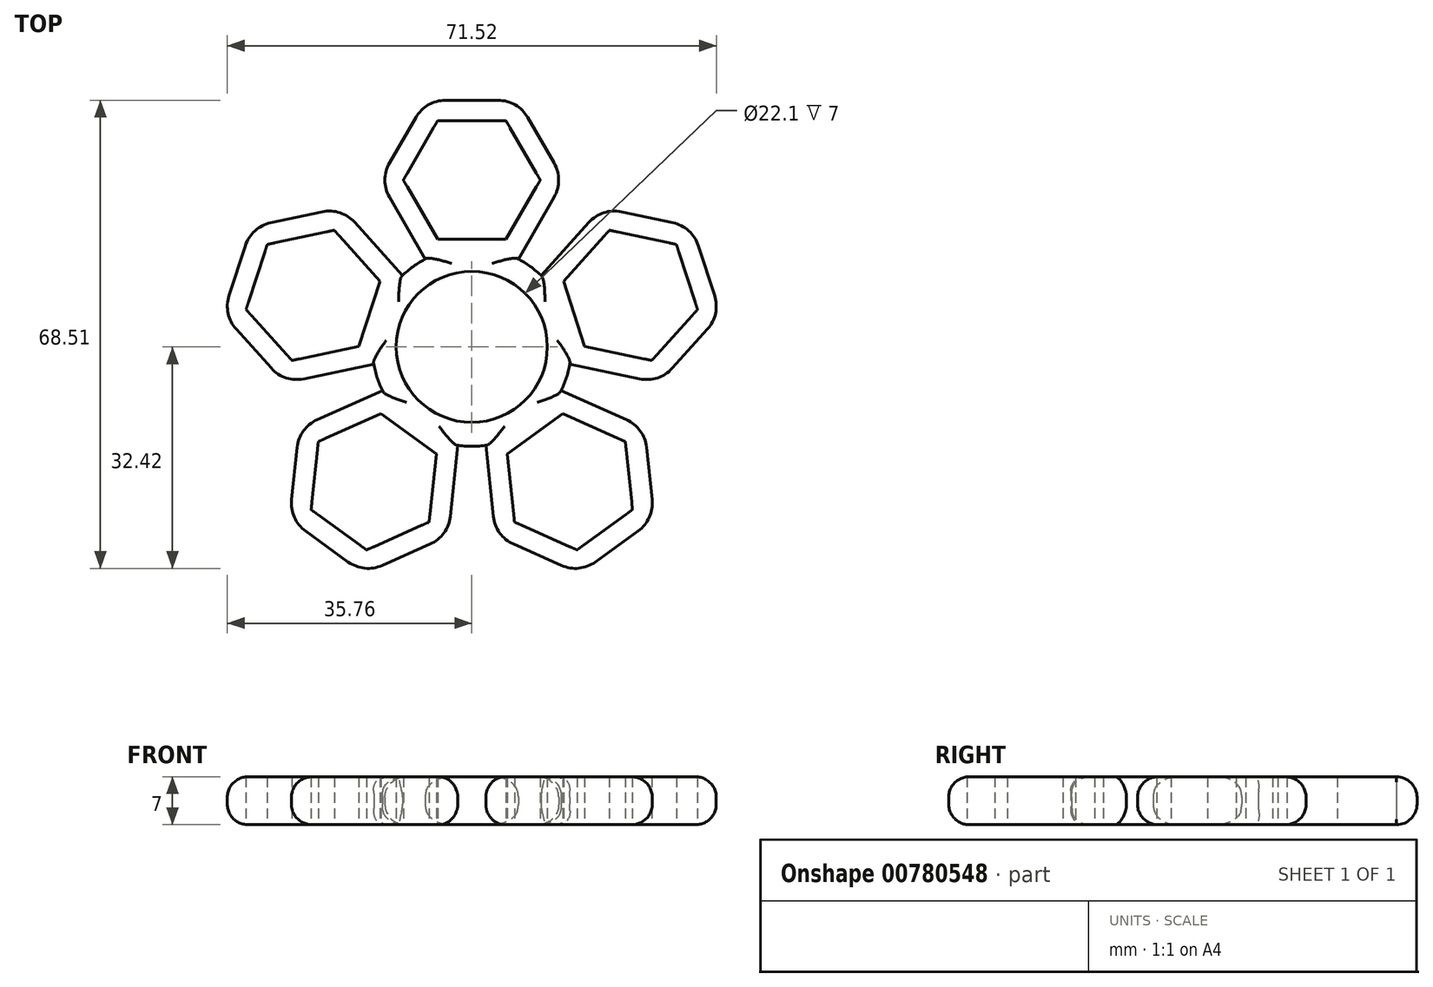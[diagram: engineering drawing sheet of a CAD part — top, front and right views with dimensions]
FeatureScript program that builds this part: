
annotation { "Feature Type Name" : "Feature", "Feature Type Description" : "" }
export const myFeature = defineFeature(function(context is Context, id is Id, definition is map)
    precondition{}
    {
        {
            var Q0;
            Q0=qCreatedBy(makeId("Top.planeOp"),FACE);
            var sketch = newSketch(context, id + "F0", { "sketchPlane" : qUnion([Q0])});
            skCircle(sketch, "E0", {"center": v(0, 0) * mm, "radius": 11.05 * mm});
            skCircle(sketch, "E1.0", {"center": v(0, 0) * mm, "radius": 14.55 * mm});
            skCircle(sketch, "E2.cCircle", {"center": v(0, 0) * mm, "radius": 19.75 * mm, "construction": true});
            skLineSegment(sketch, "E2.0", {"start": v(-23.22, 7.54) * mm, "end": v(0, 24.41) * mm, "construction": true});
            skLineSegment(sketch, "E2.1", {"start": v(0, 24.41) * mm, "end": v(23.22, 7.54) * mm, "construction": true});
            skLineSegment(sketch, "E2.2", {"start": v(23.22, 7.54) * mm, "end": v(14.35, -19.75) * mm, "construction": true});
            skLineSegment(sketch, "E2.3", {"start": v(14.35, -19.75) * mm, "end": v(-14.35, -19.75) * mm, "construction": true});
            skLineSegment(sketch, "E2.4", {"start": v(-14.35, -19.75) * mm, "end": v(-23.22, 7.54) * mm, "construction": true});
            skPoint(sketch, "E2.0.midPoint", {"position": v(-11.6, 15.98) * mm});
            skCircle(sketch, "E3.cCircle", {"center": v(0, 24.41) * mm, "radius": 8.68 * mm, "construction": true});
            skLineSegment(sketch, "E3.0", {"start": v(-5, 33.09) * mm, "end": v(5, 33.09) * mm});
            skLineSegment(sketch, "E3.1", {"start": v(5, 33.09) * mm, "end": v(10.02, 24.41) * mm});
            skLineSegment(sketch, "E3.2", {"start": v(10.02, 24.41) * mm, "end": v(5, 15.74) * mm});
            skLineSegment(sketch, "E3.3", {"start": v(5, 15.74) * mm, "end": v(-5, 15.74) * mm});
            skLineSegment(sketch, "E3.4", {"start": v(-5, 15.74) * mm, "end": v(-10.02, 24.41) * mm});
            skLineSegment(sketch, "E3.5", {"start": v(-10.02, 24.41) * mm, "end": v(-5, 33.09) * mm});
            skPoint(sketch, "E3.0.midPoint", {"position": v(0, 33.09) * mm});
            skCircle(sketch, "E4.cCircle", {"center": v(-23.22, 7.54) * mm, "radius": 8.68 * mm, "construction": true});
            skLineSegment(sketch, "E4.0", {"start": v(-33.02, 5.46) * mm, "end": v(-29.92, 14.99) * mm});
            skLineSegment(sketch, "E4.1", {"start": v(-29.92, 14.99) * mm, "end": v(-20.12, 17.07) * mm});
            skLineSegment(sketch, "E4.2", {"start": v(-20.12, 17.07) * mm, "end": v(-13.42, 9.63) * mm});
            skLineSegment(sketch, "E4.3", {"start": v(-13.42, 9.63) * mm, "end": v(-16.51, 0.1) * mm});
            skLineSegment(sketch, "E4.4", {"start": v(-16.51, 0.1) * mm, "end": v(-26.31, -1.98) * mm});
            skLineSegment(sketch, "E4.5", {"start": v(-26.31, -1.98) * mm, "end": v(-33.02, 5.46) * mm});
            skPoint(sketch, "E4.0.midPoint", {"position": v(-31.47, 10.22) * mm});
            skCircle(sketch, "E5.cCircle", {"center": v(-14.35, -19.75) * mm, "radius": 8.68 * mm, "construction": true});
            skLineSegment(sketch, "E5.0", {"start": v(-15.4, -29.71) * mm, "end": v(-23.5, -23.82) * mm});
            skLineSegment(sketch, "E5.1", {"start": v(-23.5, -23.82) * mm, "end": v(-22.45, -13.86) * mm});
            skLineSegment(sketch, "E5.2", {"start": v(-22.45, -13.86) * mm, "end": v(-13.3, -9.79) * mm});
            skLineSegment(sketch, "E5.3", {"start": v(-13.3, -9.79) * mm, "end": v(-5.2, -15.68) * mm});
            skLineSegment(sketch, "E5.4", {"start": v(-5.2, -15.68) * mm, "end": v(-6.25, -25.64) * mm});
            skLineSegment(sketch, "E5.5", {"start": v(-6.25, -25.64) * mm, "end": v(-15.4, -29.71) * mm});
            skPoint(sketch, "E5.0.midPoint", {"position": v(-19.45, -26.77) * mm});
            skCircle(sketch, "E6.cCircle", {"center": v(14.35, -19.75) * mm, "radius": 8.68 * mm, "construction": true});
            skLineSegment(sketch, "E6.0", {"start": v(23.5, -23.82) * mm, "end": v(15.4, -29.71) * mm});
            skLineSegment(sketch, "E6.1", {"start": v(15.4, -29.71) * mm, "end": v(6.25, -25.64) * mm});
            skLineSegment(sketch, "E6.2", {"start": v(6.25, -25.64) * mm, "end": v(5.2, -15.68) * mm});
            skLineSegment(sketch, "E6.3", {"start": v(5.2, -15.68) * mm, "end": v(13.3, -9.79) * mm});
            skLineSegment(sketch, "E6.4", {"start": v(13.3, -9.79) * mm, "end": v(22.45, -13.86) * mm});
            skLineSegment(sketch, "E6.5", {"start": v(22.45, -13.86) * mm, "end": v(23.5, -23.82) * mm});
            skPoint(sketch, "E6.0.midPoint", {"position": v(19.45, -26.77) * mm});
            skCircle(sketch, "E7.cCircle", {"center": v(23.22, 7.54) * mm, "radius": 8.68 * mm, "construction": true});
            skLineSegment(sketch, "E7.0", {"start": v(29.92, 14.99) * mm, "end": v(33.02, 5.46) * mm});
            skLineSegment(sketch, "E7.1", {"start": v(33.02, 5.46) * mm, "end": v(26.31, -1.98) * mm});
            skLineSegment(sketch, "E7.2", {"start": v(26.31, -1.98) * mm, "end": v(16.51, 0.1) * mm});
            skLineSegment(sketch, "E7.3", {"start": v(16.51, 0.1) * mm, "end": v(13.42, 9.63) * mm});
            skLineSegment(sketch, "E7.4", {"start": v(13.42, 9.63) * mm, "end": v(20.12, 17.07) * mm});
            skLineSegment(sketch, "E7.5", {"start": v(20.12, 17.07) * mm, "end": v(29.92, 14.99) * mm});
            skPoint(sketch, "E7.0.midPoint", {"position": v(31.47, 10.22) * mm});
            skLineSegment(sketch, "E8.0", {"start": v(10.03, 10.35) * mm, "end": v(19.05, 20.37) * mm});
            skLineSegment(sketch, "E8.1", {"start": v(32.24, 17.56) * mm, "end": v(36.4, 4.74) * mm});
            skLineSegment(sketch, "E8.2", {"start": v(36.4, 4.74) * mm, "end": v(27.38, -5.28) * mm});
            skLineSegment(sketch, "E8.3", {"start": v(19.05, 20.37) * mm, "end": v(32.24, 17.56) * mm});
            skLineSegment(sketch, "E8.4", {"start": v(27.38, -5.28) * mm, "end": v(14.2, -2.47) * mm});
            skLineSegment(sketch, "E8.5", {"start": v(14.2, -2.47) * mm, "end": v(10.03, 10.35) * mm});
            skLineSegment(sketch, "E9.0", {"start": v(-13.48, 24.41) * mm, "end": v(-6.74, 36.09) * mm});
            skLineSegment(sketch, "E9.1", {"start": v(6.74, 36.09) * mm, "end": v(13.48, 24.41) * mm});
            skLineSegment(sketch, "E9.2", {"start": v(13.48, 24.41) * mm, "end": v(6.74, 12.74) * mm});
            skLineSegment(sketch, "E9.3", {"start": v(-6.74, 36.09) * mm, "end": v(6.74, 36.09) * mm});
            skLineSegment(sketch, "E9.4", {"start": v(6.74, 12.74) * mm, "end": v(-6.74, 12.74) * mm});
            skLineSegment(sketch, "E9.5", {"start": v(-6.74, 12.74) * mm, "end": v(-13.48, 24.41) * mm});
            skLineSegment(sketch, "E10.0", {"start": v(-36.4, 4.74) * mm, "end": v(-32.24, 17.56) * mm});
            skLineSegment(sketch, "E10.1", {"start": v(-19.05, 20.37) * mm, "end": v(-10.03, 10.35) * mm});
            skLineSegment(sketch, "E10.2", {"start": v(-10.03, 10.35) * mm, "end": v(-14.2, -2.47) * mm});
            skLineSegment(sketch, "E10.3", {"start": v(-32.24, 17.56) * mm, "end": v(-19.05, 20.37) * mm});
            skLineSegment(sketch, "E10.4", {"start": v(-14.2, -2.47) * mm, "end": v(-27.38, -5.28) * mm});
            skLineSegment(sketch, "E10.5", {"start": v(-27.38, -5.28) * mm, "end": v(-36.4, 4.74) * mm});
            skLineSegment(sketch, "E11.0", {"start": v(-26.66, -25.23) * mm, "end": v(-25.26, -11.83) * mm});
            skLineSegment(sketch, "E11.1", {"start": v(-12.94, -6.34) * mm, "end": v(-2.03, -14.27) * mm});
            skLineSegment(sketch, "E11.2", {"start": v(-2.03, -14.27) * mm, "end": v(-3.44, -27.67) * mm});
            skLineSegment(sketch, "E11.3", {"start": v(-25.26, -11.83) * mm, "end": v(-12.94, -6.34) * mm});
            skLineSegment(sketch, "E11.4", {"start": v(-3.44, -27.67) * mm, "end": v(-15.76, -33.16) * mm});
            skLineSegment(sketch, "E11.5", {"start": v(-15.76, -33.16) * mm, "end": v(-26.66, -25.23) * mm});
            skLineSegment(sketch, "E12.0", {"start": v(3.44, -27.67) * mm, "end": v(2.03, -14.27) * mm});
            skLineSegment(sketch, "E12.1", {"start": v(12.94, -6.34) * mm, "end": v(25.26, -11.83) * mm});
            skLineSegment(sketch, "E12.2", {"start": v(25.26, -11.83) * mm, "end": v(26.66, -25.23) * mm});
            skLineSegment(sketch, "E12.3", {"start": v(2.03, -14.27) * mm, "end": v(12.94, -6.34) * mm});
            skLineSegment(sketch, "E12.4", {"start": v(26.66, -25.23) * mm, "end": v(15.76, -33.16) * mm});
            skLineSegment(sketch, "E12.5", {"start": v(15.76, -33.16) * mm, "end": v(3.44, -27.67) * mm});
            skSolve(sketch);
        }
        {
            var Q0;
            Q0=qSketchRegion(id+"F0",true);
            extrude(context, id + "F1", {"entities" : qUnion([Q0]), "depth" : 7 * mm, "offsetDistance" : 25 * mm});
        }
        {
            var Q0;
            Q0=makeQuery(id+"F1.opExtrude","SWEPT_EDGE",EDGE,{"disambiguationData":[OSD([sQuery(id+"F0.wireOp",EDGE,"E12.0"),sQuery(id+"F0.wireOp",EDGE,"E12.5")])]});
            var Q1;
            Q1=makeQuery(id+"F1.opExtrude","SWEPT_EDGE",EDGE,{"disambiguationData":[OSD([sQuery(id+"F0.wireOp",EDGE,"E12.2"),sQuery(id+"F0.wireOp",EDGE,"E12.4")])]});
            var Q2;
            Q2=makeQuery(id+"F1.opExtrude","SWEPT_EDGE",EDGE,{"disambiguationData":[OSD([sQuery(id+"F0.wireOp",EDGE,"E12.1"),sQuery(id+"F0.wireOp",EDGE,"E12.2")])]});
            var Q3;
            Q3=makeQuery(id+"F1.opExtrude","SWEPT_EDGE",EDGE,{"disambiguationData":[OSD([sQuery(id+"F0.wireOp",EDGE,"E8.2"),sQuery(id+"F0.wireOp",EDGE,"E8.4")])]});
            var Q4;
            Q4=makeQuery(id+"F1.opExtrude","SWEPT_EDGE",EDGE,{"disambiguationData":[OSD([sQuery(id+"F0.wireOp",EDGE,"E8.1"),sQuery(id+"F0.wireOp",EDGE,"E8.2")])]});
            var Q5;
            Q5=makeQuery(id+"F1.opExtrude","SWEPT_EDGE",EDGE,{"disambiguationData":[OSD([sQuery(id+"F0.wireOp",EDGE,"E8.1"),sQuery(id+"F0.wireOp",EDGE,"E8.3")])]});
            var Q6;
            Q6=makeQuery(id+"F1.opExtrude","SWEPT_EDGE",EDGE,{"disambiguationData":[OSD([sQuery(id+"F0.wireOp",EDGE,"E8.0"),sQuery(id+"F0.wireOp",EDGE,"E8.3")])]});
            var Q7;
            Q7=makeQuery(id+"F1.opExtrude","SWEPT_EDGE",EDGE,{"disambiguationData":[OSD([sQuery(id+"F0.wireOp",EDGE,"E9.1"),sQuery(id+"F0.wireOp",EDGE,"E9.2")])]});
            var Q8;
            Q8=makeQuery(id+"F1.opExtrude","SWEPT_EDGE",EDGE,{"disambiguationData":[OSD([sQuery(id+"F0.wireOp",EDGE,"E9.1"),sQuery(id+"F0.wireOp",EDGE,"E9.3")])]});
            var Q9;
            Q9=makeQuery(id+"F1.opExtrude","SWEPT_EDGE",EDGE,{"disambiguationData":[OSD([sQuery(id+"F0.wireOp",EDGE,"E9.0"),sQuery(id+"F0.wireOp",EDGE,"E9.3")])]});
            var Q10;
            Q10=makeQuery(id+"F1.opExtrude","SWEPT_EDGE",EDGE,{"disambiguationData":[OSD([sQuery(id+"F0.wireOp",EDGE,"E9.0"),sQuery(id+"F0.wireOp",EDGE,"E9.5")])]});
            var Q11;
            Q11=makeQuery(id+"F1.opExtrude","SWEPT_EDGE",EDGE,{"disambiguationData":[OSD([sQuery(id+"F0.wireOp",EDGE,"E10.1"),sQuery(id+"F0.wireOp",EDGE,"E10.3")])]});
            var Q12;
            Q12=makeQuery(id+"F1.opExtrude","SWEPT_EDGE",EDGE,{"disambiguationData":[OSD([sQuery(id+"F0.wireOp",EDGE,"E10.0"),sQuery(id+"F0.wireOp",EDGE,"E10.3")])]});
            var Q13;
            Q13=makeQuery(id+"F1.opExtrude","SWEPT_EDGE",EDGE,{"disambiguationData":[OSD([sQuery(id+"F0.wireOp",EDGE,"E10.0"),sQuery(id+"F0.wireOp",EDGE,"E10.5")])]});
            var Q14;
            Q14=makeQuery(id+"F1.opExtrude","SWEPT_EDGE",EDGE,{"disambiguationData":[OSD([sQuery(id+"F0.wireOp",EDGE,"E10.4"),sQuery(id+"F0.wireOp",EDGE,"E10.5")])]});
            var Q15;
            Q15=makeQuery(id+"F1.opExtrude","SWEPT_EDGE",EDGE,{"disambiguationData":[OSD([sQuery(id+"F0.wireOp",EDGE,"E11.0"),sQuery(id+"F0.wireOp",EDGE,"E11.3")])]});
            var Q16;
            Q16=makeQuery(id+"F1.opExtrude","SWEPT_EDGE",EDGE,{"disambiguationData":[OSD([sQuery(id+"F0.wireOp",EDGE,"E11.0"),sQuery(id+"F0.wireOp",EDGE,"E11.5")])]});
            var Q17;
            Q17=makeQuery(id+"F1.opExtrude","SWEPT_EDGE",EDGE,{"disambiguationData":[OSD([sQuery(id+"F0.wireOp",EDGE,"E11.4"),sQuery(id+"F0.wireOp",EDGE,"E11.5")])]});
            var Q18;
            Q18=makeQuery(id+"F1.opExtrude","SWEPT_EDGE",EDGE,{"disambiguationData":[OSD([sQuery(id+"F0.wireOp",EDGE,"E11.2"),sQuery(id+"F0.wireOp",EDGE,"E11.4")])]});
            var Q19;
            Q19=makeQuery(id+"F1.opExtrude","SWEPT_EDGE",EDGE,{"disambiguationData":[OSD([sQuery(id+"F0.wireOp",EDGE,"E12.4"),sQuery(id+"F0.wireOp",EDGE,"E12.5")])]});
            fillet(context, id + "F2", {"entities" : qUnion([Q0, Q1, Q2, Q3, Q4, Q5, Q6, Q7, Q8, Q9, Q10, Q11, Q12, Q13, Q14, Q15, Q16, Q17, Q18, Q19]), "radius" : 5 * mm, "tangentPropagation" : true, "allowEdgeOverflow" : false});
        }
        {
            var Q0;
            Q0=makeQuery(id+"F1.opExtrude","CAP_EDGE",EDGE,{"disambiguationData":[OSD([sQuery(id+"F0.wireOp",EDGE,"E11.4")])],"isStart":true});
            var Q1;
            Q1=makeQuery(id+"F1.opExtrude","CAP_EDGE",EDGE,{"disambiguationData":[OSD([sQuery(id+"F0.wireOp",EDGE,"E12.5")])],"isStart":true});
            var Q2;
            Q2=makeQuery(id+"F1.opExtrude","CAP_EDGE",EDGE,{"disambiguationData":[OSD([sQuery(id+"F0.wireOp",EDGE,"E8.2")])],"isStart":true});
            var Q3;
            Q3=makeQuery(id+"F1.opExtrude","CAP_EDGE",EDGE,{"disambiguationData":[OSD([sQuery(id+"F0.wireOp",EDGE,"E9.2")])],"isStart":true});
            var Q4;
            Q4=makeQuery(id+"F1.opExtrude","CAP_EDGE",EDGE,{"disambiguationData":[OSD([sQuery(id+"F0.wireOp",EDGE,"E10.3")])],"isStart":true});
            var Q5;
            Q5=makeQuery(id+"F1.opExtrude","CAP_EDGE",EDGE,{"disambiguationData":[OSD([sQuery(id+"F0.wireOp",EDGE,"E8.1")])],"isStart":false});
            var Q6;
            Q6=makeQuery(id+"F1.opExtrude","CAP_EDGE",EDGE,{"disambiguationData":[OSD([sQuery(id+"F0.wireOp",EDGE,"E12.2")])],"isStart":false});
            var Q7;
            Q7=makeQuery(id+"F1.opExtrude","CAP_EDGE",EDGE,{"disambiguationData":[OSD([sQuery(id+"F0.wireOp",EDGE,"E11.5")])],"isStart":false});
            var Q8;
            Q8=makeQuery(id+"F1.opExtrude","CAP_EDGE",EDGE,{"disambiguationData":[OSD([sQuery(id+"F0.wireOp",EDGE,"E10.5")])],"isStart":false});
            var Q9;
            Q9=makeQuery(id+"F1.opExtrude","CAP_EDGE",EDGE,{"disambiguationData":[OSD([sQuery(id+"F0.wireOp",EDGE,"E9.0")])],"isStart":false});
            fillet(context, id + "F3", {"entities" : qUnion([Q0, Q1, Q2, Q3, Q4, Q5, Q6, Q7, Q8, Q9]), "radius" : 3 * mm, "tangentPropagation" : true, "allowEdgeOverflow" : false});
        }
        {
            var Q0;
            {var subQ0=sQuery(id+"F0.wireOp",EDGE,"E1.0");Q0=makeQuery(id+"F1.opExtrude","CAP_EDGE",EDGE,{"disambiguationData":[OSD([subQ0]),TDD([makeQuery(id+"F0.imprint","IMPRINT",EDGE,{"disambiguationData":[TD([[makeQuery(id+"F0.imprint","INTERSECT",VERTEX,{"derivedFrom":[subQ0,sQuery(id+"F0.wireOp",EDGE,"E11.2")]}),-1.0]])],"derivedFrom":subQ0})])],"isStart":false});}
            var Q1;
            {var subQ0=sQuery(id+"F0.wireOp",EDGE,"E1.0");Q1=makeQuery(id+"F1.opExtrude","CAP_EDGE",EDGE,{"disambiguationData":[OSD([subQ0]),TDD([makeQuery(id+"F0.imprint","IMPRINT",EDGE,{"disambiguationData":[TD([[makeQuery(id+"F0.imprint","INTERSECT",VERTEX,{"derivedFrom":[subQ0,sQuery(id+"F0.wireOp",EDGE,"E12.1")]}),-1.0]])],"derivedFrom":subQ0})])],"isStart":false});}
            var Q2;
            {var subQ0=sQuery(id+"F0.wireOp",EDGE,"E1.0");Q2=makeQuery(id+"F1.opExtrude","CAP_EDGE",EDGE,{"disambiguationData":[OSD([subQ0]),TDD([makeQuery(id+"F0.imprint","IMPRINT",EDGE,{"disambiguationData":[TD([[makeQuery(id+"F0.imprint","INTERSECT",VERTEX,{"derivedFrom":[subQ0,sQuery(id+"F0.wireOp",EDGE,"E9.2")]}),1.0]])],"derivedFrom":subQ0})])],"isStart":false});}
            var Q3;
            {var subQ0=sQuery(id+"F0.wireOp",EDGE,"E1.0");Q3=makeQuery(id+"F1.opExtrude","CAP_EDGE",EDGE,{"disambiguationData":[OSD([subQ0]),TDD([makeQuery(id+"F0.imprint","IMPRINT",EDGE,{"disambiguationData":[TD([[makeQuery(id+"F0.imprint","INTERSECT",VERTEX,{"derivedFrom":[subQ0,sQuery(id+"F0.wireOp",EDGE,"E9.5")]}),-1.0]])],"derivedFrom":subQ0})])],"isStart":false});}
            var Q4;
            {var subQ0=sQuery(id+"F0.wireOp",EDGE,"E1.0");Q4=makeQuery(id+"F1.opExtrude","CAP_EDGE",EDGE,{"disambiguationData":[OSD([subQ0]),TDD([makeQuery(id+"F0.imprint","IMPRINT",EDGE,{"disambiguationData":[TD([[makeQuery(id+"F0.imprint","INTERSECT",VERTEX,{"derivedFrom":[subQ0,sQuery(id+"F0.wireOp",EDGE,"E10.4")]}),-1.0]])],"derivedFrom":subQ0})])],"isStart":false});}
            var Q5;
            {var subQ0=sQuery(id+"F0.wireOp",EDGE,"E1.0");Q5=makeQuery(id+"F1.opExtrude","CAP_EDGE",EDGE,{"disambiguationData":[OSD([subQ0]),TDD([makeQuery(id+"F0.imprint","IMPRINT",EDGE,{"disambiguationData":[TD([[makeQuery(id+"F0.imprint","INTERSECT",VERTEX,{"derivedFrom":[subQ0,sQuery(id+"F0.wireOp",EDGE,"E11.2")]}),-1.0]])],"derivedFrom":subQ0})])],"isStart":true});}
            var Q6;
            {var subQ0=sQuery(id+"F0.wireOp",EDGE,"E1.0");Q6=makeQuery(id+"F1.opExtrude","CAP_EDGE",EDGE,{"disambiguationData":[OSD([subQ0]),TDD([makeQuery(id+"F0.imprint","IMPRINT",EDGE,{"disambiguationData":[TD([[makeQuery(id+"F0.imprint","INTERSECT",VERTEX,{"derivedFrom":[subQ0,sQuery(id+"F0.wireOp",EDGE,"E12.1")]}),-1.0]])],"derivedFrom":subQ0})])],"isStart":true});}
            var Q7;
            {var subQ0=sQuery(id+"F0.wireOp",EDGE,"E1.0");Q7=makeQuery(id+"F1.opExtrude","CAP_EDGE",EDGE,{"disambiguationData":[OSD([subQ0]),TDD([makeQuery(id+"F0.imprint","IMPRINT",EDGE,{"disambiguationData":[TD([[makeQuery(id+"F0.imprint","INTERSECT",VERTEX,{"derivedFrom":[subQ0,sQuery(id+"F0.wireOp",EDGE,"E9.2")]}),1.0]])],"derivedFrom":subQ0})])],"isStart":true});}
            var Q8;
            {var subQ0=sQuery(id+"F0.wireOp",EDGE,"E1.0");Q8=makeQuery(id+"F1.opExtrude","CAP_EDGE",EDGE,{"disambiguationData":[OSD([subQ0]),TDD([makeQuery(id+"F0.imprint","IMPRINT",EDGE,{"disambiguationData":[TD([[makeQuery(id+"F0.imprint","INTERSECT",VERTEX,{"derivedFrom":[subQ0,sQuery(id+"F0.wireOp",EDGE,"E9.5")]}),-1.0]])],"derivedFrom":subQ0})])],"isStart":true});}
            var Q9;
            {var subQ0=sQuery(id+"F0.wireOp",EDGE,"E1.0");Q9=makeQuery(id+"F1.opExtrude","CAP_EDGE",EDGE,{"disambiguationData":[OSD([subQ0]),TDD([makeQuery(id+"F0.imprint","IMPRINT",EDGE,{"disambiguationData":[TD([[makeQuery(id+"F0.imprint","INTERSECT",VERTEX,{"derivedFrom":[subQ0,sQuery(id+"F0.wireOp",EDGE,"E10.4")]}),-1.0]])],"derivedFrom":subQ0})])],"isStart":true});}
            fillet(context, id + "F4", {"entities" : qUnion([Q0, Q1, Q2, Q3, Q4, Q5, Q6, Q7, Q8, Q9]), "radius" : 2 * mm, "tangentPropagation" : true, "allowEdgeOverflow" : false});
        }
    });
